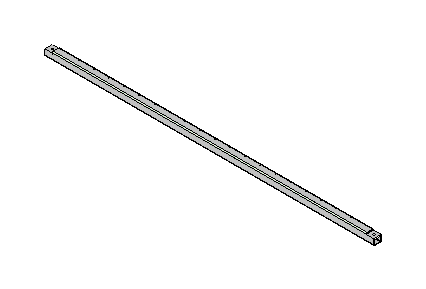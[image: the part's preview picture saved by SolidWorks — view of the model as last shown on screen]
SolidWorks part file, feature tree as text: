
SOLIDWORKS PART (.sldprt)
format: sldprt  version: not decoded by parser v0  size: 244,736 bytes
history: native  units: mm
features: sketch x5, cut_extrude x3, extrude x2, shell x1, pattern_linear x1 (+11 scaffold rows collapsed)
feature tree (23):
  scaffold x11  (default folders/planes/origin — collapsed)
  sketch  "Sketch1"  dims[D3=4.7625mm D1=38.1mm D2=38.1mm]
  extrude  "Extrude1"  Depth=1657.35mm
  shell  "Shell1"  Thickness=2.54mm
  sketch  "Sketch2"
  cut_extrude  "Cut-Extrude1"  Depth=6.35mm
  sketch  "Sketch3"
  extrude  "Extrude2"  Depth=6.35mm
  sketch  "Sketch4"  dims[D1=9.525mm D2=9.525mm]
  cut_extrude  "Cut-Extrude2"  [1 undecoded]
  sketch  "Sketch5"  dims[D1=3.175mm D2=76.2mm]
  cut_extrude  "Cut-Extrude3"  Depth=9.525mm
  pattern_linear  "LPattern2"  Count1=10 Count2=10 Spacing1=76.2mm Spacing2=76.2mm
decode coverage: 9 of 12 modeling features carry decoded parameters
note: 1 parameter value undecoded
note: suppression state not decoded; provenance and decode notes live in map.json
